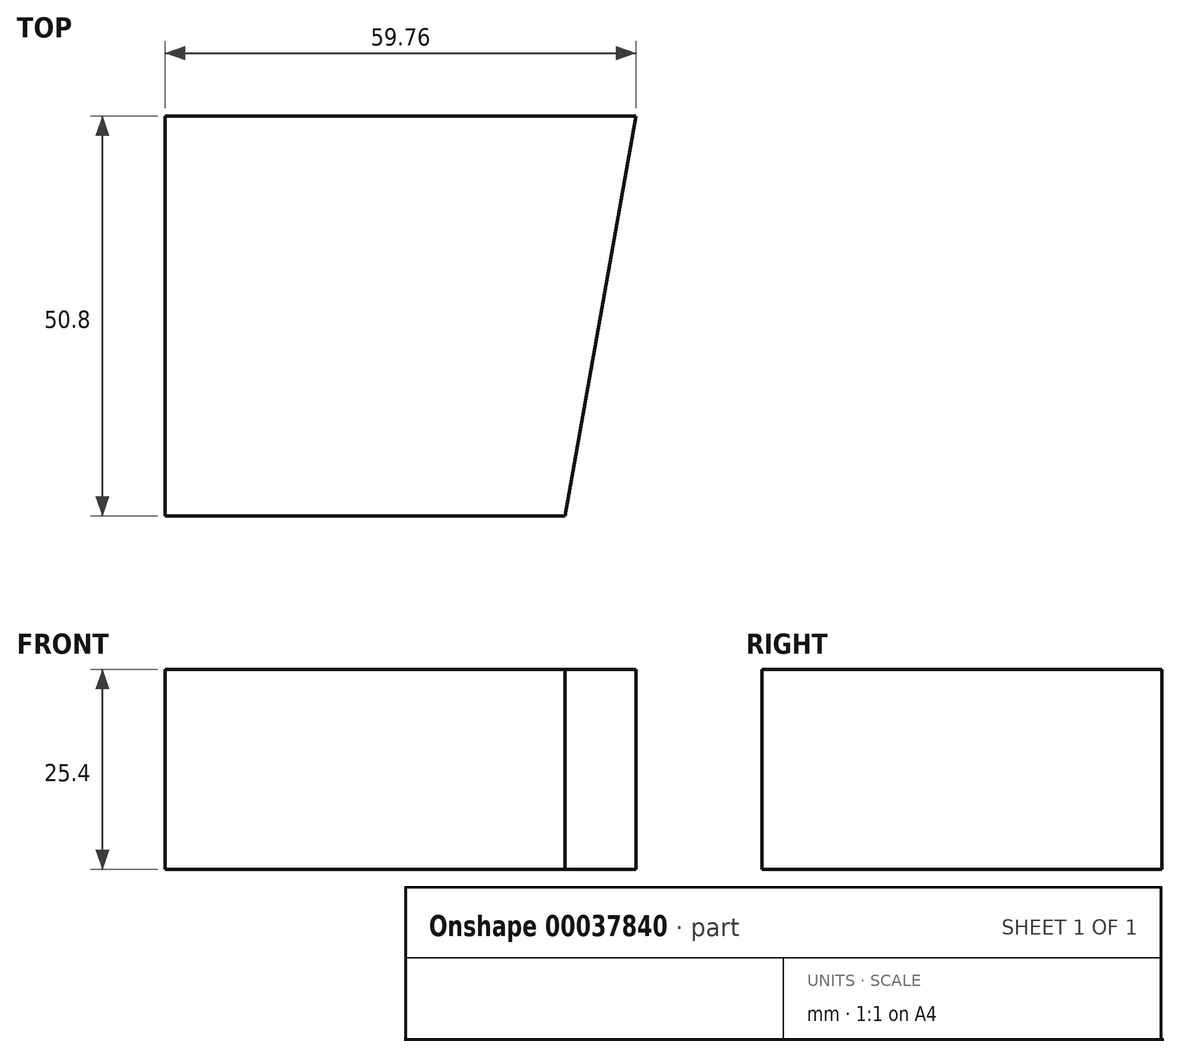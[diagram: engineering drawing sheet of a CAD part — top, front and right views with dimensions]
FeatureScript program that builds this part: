
annotation { "Feature Type Name" : "Feature", "Feature Type Description" : "" }
export const myFeature = defineFeature(function(context is Context, id is Id, definition is map)
    precondition{}
    {
        {
            var Q0;
            Q0=qCreatedBy(makeId("Top.planeOp"),FACE);
            var sketch = newSketch(context, id + "F0", { "sketchPlane" : qUnion([Q0])});
            skLineSegment(sketch, "E0.bottom", {"start": v(0, 0) * mm, "end": v(59.76, 0) * mm});
            skLineSegment(sketch, "E0.top", {"start": v(0, -50.8) * mm, "end": v(50.8, -50.8) * mm});
            skLineSegment(sketch, "E0.left", {"start": v(0, 0) * mm, "end": v(0, -50.8) * mm});
            skLineSegment(sketch, "E0.right", {"start": v(59.76, 0) * mm, "end": v(50.8, -50.8) * mm});
            skLineSegment(sketch, "E1", {"start": v(50.8, -50.8) * mm, "end": v(50.8, 0) * mm, "construction": true});
            skSolve(sketch);
        }
        {
            var Q0;
            Q0 = qSketchRegion(id + "F0", true);
            extrude(context, id + "F1", {"entities" : qUnion([Q0]), "depth" : 25.4 * mm});
        }
    });
